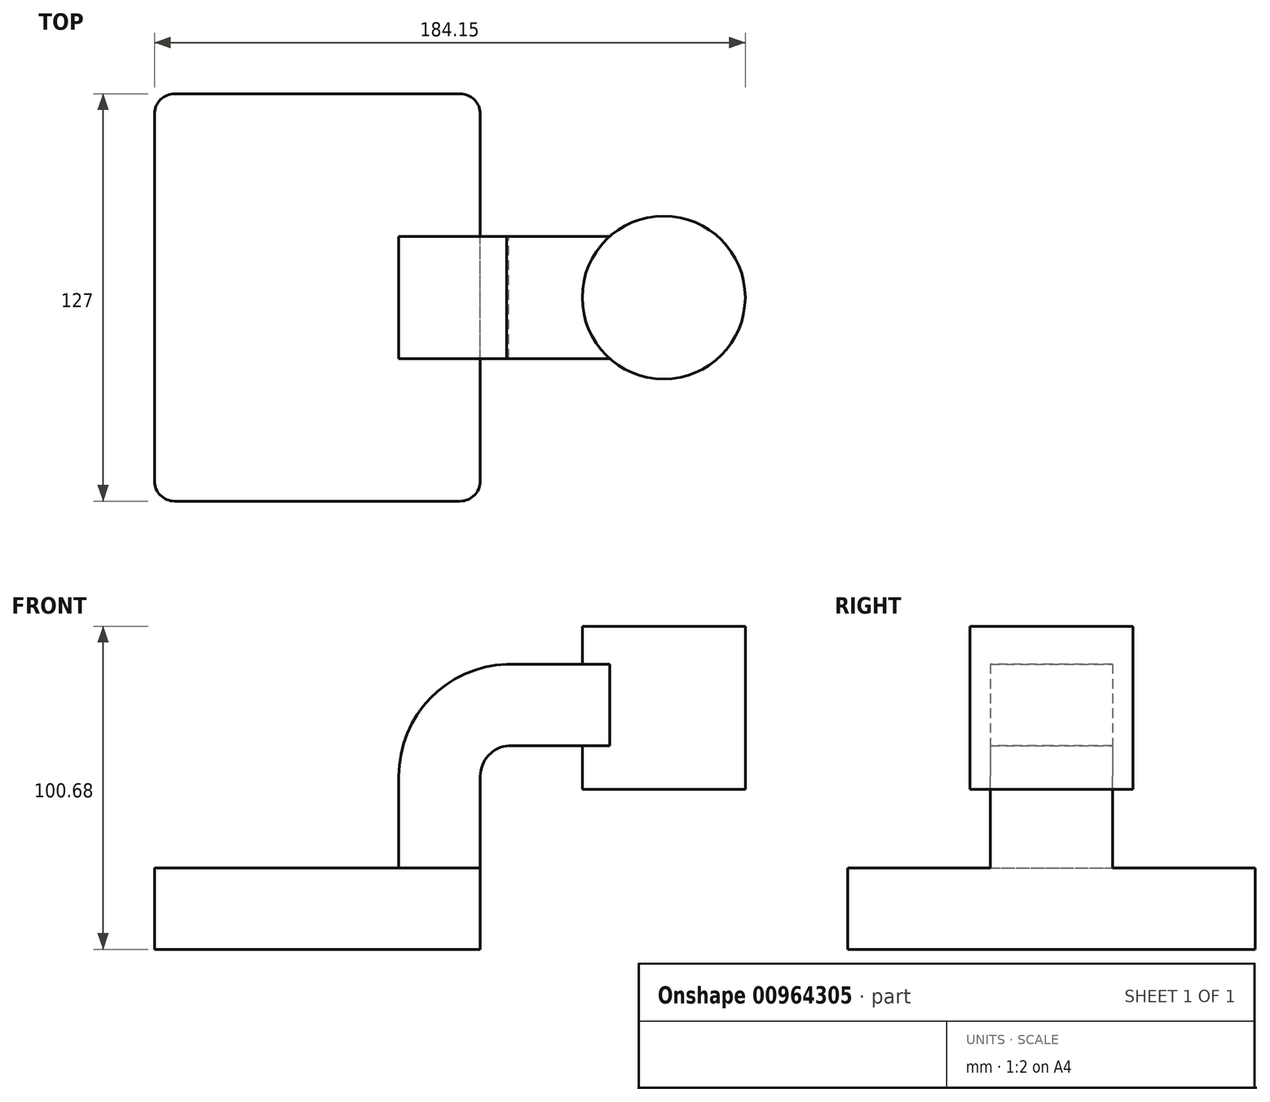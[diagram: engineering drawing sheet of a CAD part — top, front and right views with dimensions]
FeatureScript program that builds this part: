
annotation { "Feature Type Name" : "Feature", "Feature Type Description" : "" }
export const myFeature = defineFeature(function(context is Context, id is Id, definition is map)
    precondition{}
    {
        {
            var Q0;
            Q0=qCreatedBy(makeId("Front.planeOp"),FACE);
            var sketch = newSketch(context, id + "F0", { "sketchPlane" : qUnion([Q0])});
            skLineSegment(sketch, "E0.bottom", {"start": v(-50.8, -12.7) * mm, "end": v(50.8, -12.7) * mm});
            skLineSegment(sketch, "E0.top", {"start": v(-50.8, 12.7) * mm, "end": v(50.8, 12.7) * mm});
            skLineSegment(sketch, "E0.left", {"start": v(-50.8, -12.7) * mm, "end": v(-50.8, 12.7) * mm});
            skLineSegment(sketch, "E0.right", {"start": v(50.8, -12.7) * mm, "end": v(50.8, 12.7) * mm});
            skPoint(sketch, "E0.middle", {"position": v(0, 0) * mm});
            skLineSegment(sketch, "E1.bottom", {"start": v(133.35, 37.18) * mm, "end": v(82.55, 37.18) * mm});
            skLineSegment(sketch, "E1.top", {"start": v(133.35, 87.98) * mm, "end": v(82.55, 87.98) * mm});
            skLineSegment(sketch, "E1.left", {"start": v(133.35, 37.18) * mm, "end": v(133.35, 87.98) * mm});
            skLineSegment(sketch, "E1.right", {"start": v(82.55, 37.18) * mm, "end": v(82.55, 87.98) * mm});
            skPoint(sketch, "E1.middle", {"position": v(107.95, 62.58) * mm});
            skLineSegment(sketch, "E2", {"start": v(50.8, 12.7) * mm, "end": v(50.8, 41.27) * mm});
            skArc(sketch, "E3", {"start": v(50.8, 41.27) * mm, "mid": v(53.36, 47.77) * mm, "end": v(59.65, 50.78) * mm});
            skPoint(sketch, "E4.endSnap0", {"position": v(53.36, 47.77) * mm});
            skLineSegment(sketch, "E5", {"start": v(59.65, 50.78) * mm, "end": v(107.95, 50.78) * mm});
            skLineSegment(sketch, "E6.0", {"start": v(59.03, 76.18) * mm, "end": v(107.95, 76.18) * mm});
            skArc(sketch, "E6.1", {"start": v(25.4, 41.27) * mm, "mid": v(35.18, 65.5) * mm, "end": v(59.03, 76.18) * mm});
            skLineSegment(sketch, "E6.2", {"start": v(25.4, 12.7) * mm, "end": v(25.4, 41.27) * mm});
            skPoint(sketch, "E7.1.internal.snap0", {"position": v(83.5, 76.18) * mm});
            skFitSpline(sketch, "E8", {"points": [v(-50.8, 12.7) * mm, v(59.03, 76.18) * mm], "startDerivative": vector(0.25, 91.43) * mm, "endDerivative": vector(129, 0.25) * mm});
            skPoint(sketch, "E9", {"position": v(107.95, 37.18) * mm});
            skLineSegment(sketch, "E10", {"start": v(107.95, 37.18) * mm, "end": v(107.95, 87.98) * mm});
            skSolve(sketch);
        }
        {
            var Q0;
            Q0=makeQuery(id+"F0.imprint","IMPRINT",FACE,{"disambiguationData":[TD([[makeQuery(id+"F0.imprint","IMPRINT",EDGE,{"derivedFrom":sQuery(id+"F0.wireOp",EDGE,"E0.bottom")}),1.0]])]});
            extrude(context, id + "F1", {"entities" : qUnion([Q0]), "endBound" : BoundingType.SYMMETRIC, "depth" : 127 * mm, "offsetDistance" : 25.4 * mm});
        }
        {
            var Q0;
            {var subQ1=sQuery(id+"F0.wireOp",EDGE,"E2");Q0=makeQuery(id+"F0.imprint","IMPRINT",FACE,{"disambiguationData":[TD([[makeQuery(id+"F0.imprint","IMPRINT",EDGE,{"derivedFrom":subQ1}),1.0]])]});}
            var Q1;
            {var subQ0=sQuery(id+"F0.wireOp",EDGE,"E5");var subQ1=sQuery(id+"F0.wireOp",EDGE,"E1.right");var subQ2=makeQuery(id+"F0.imprint","INTERSECT",VERTEX,{"derivedFrom":[subQ1,subQ0]});Q1=makeQuery(id+"F0.imprint","IMPRINT",FACE,{"disambiguationData":[TD([[makeQuery(id+"F0.imprint","IMPRINT",EDGE,{"disambiguationData":[TD([[subQ2,-1.0]])],"derivedFrom":subQ1}),-1.0]])]});}
            extrude(context, id + "F2", {"entities" : qUnion([Q0, Q1]), "operationType" : NewBodyOperationType.ADD, "endBound" : BoundingType.SYMMETRIC, "depth" : 38.1 * mm, "offsetDistance" : 25.4 * mm});
        }
        {
            var Q0;
            {var subQ0=sQuery(id+"F0.wireOp",EDGE,"E1.left");Q0=makeQuery(id+"F0.imprint","IMPRINT",FACE,{"disambiguationData":[TD([[makeQuery(id+"F0.imprint","IMPRINT",EDGE,{"derivedFrom":subQ0}),1.0]])]});}
            var Q1;
            Q1=sQuery(id+"F0.wireOp",EDGE,"E10");
            revolve(context, id + "F3", {"operationType" : NewBodyOperationType.ADD, "surfaceOperationType" : NewSurfaceOperationType.NEW, "entities" : qUnion([Q0]), "axis" : qUnion([Q1]), "revolveType" : RevolveType.FULL});
        }
        {
            var Q0;
            Q0=makeQuery(id+"F0.imprint","IMPRINT",FACE,{"disambiguationData":[TD([[makeQuery(id+"F0.imprint","IMPRINT",EDGE,{"derivedFrom":sQuery(id+"F0.wireOp",EDGE,"E6.1")}),1.0]])]});
            extrude(context, id + "F4", {"entities" : qUnion([Q0]), "operationType" : NewBodyOperationType.ADD, "endBound" : BoundingType.SYMMETRIC, "depth" : 25.4 * mm, "offsetDistance" : 25.4 * mm});
        }
        {
            var Q0;
            Q0=makeQuery(id+"F1.opExtrude","CAP_EDGE",EDGE,{"disambiguationData":[OSD([sQuery(id+"F0.wireOp",EDGE,"E0.right")])],"isStart":false});
            var Q1;
            Q1=makeQuery(id+"F1.opExtrude","CAP_EDGE",EDGE,{"disambiguationData":[OSD([sQuery(id+"F0.wireOp",EDGE,"E0.left")])],"isStart":false});
            var Q2;
            Q2=makeQuery(id+"F1.opExtrude","CAP_EDGE",EDGE,{"disambiguationData":[OSD([sQuery(id+"F0.wireOp",EDGE,"E0.left")])],"isStart":true});
            var Q3;
            Q3=makeQuery(id+"F1.opExtrude","CAP_EDGE",EDGE,{"disambiguationData":[OSD([sQuery(id+"F0.wireOp",EDGE,"E0.right")])],"isStart":true});
            fillet(context, id + "F5", {"entities" : qUnion([Q0, Q1, Q2, Q3]), "radius" : 6.35 * mm, "tangentPropagation" : true, "allowEdgeOverflow" : false});
        }
    });
